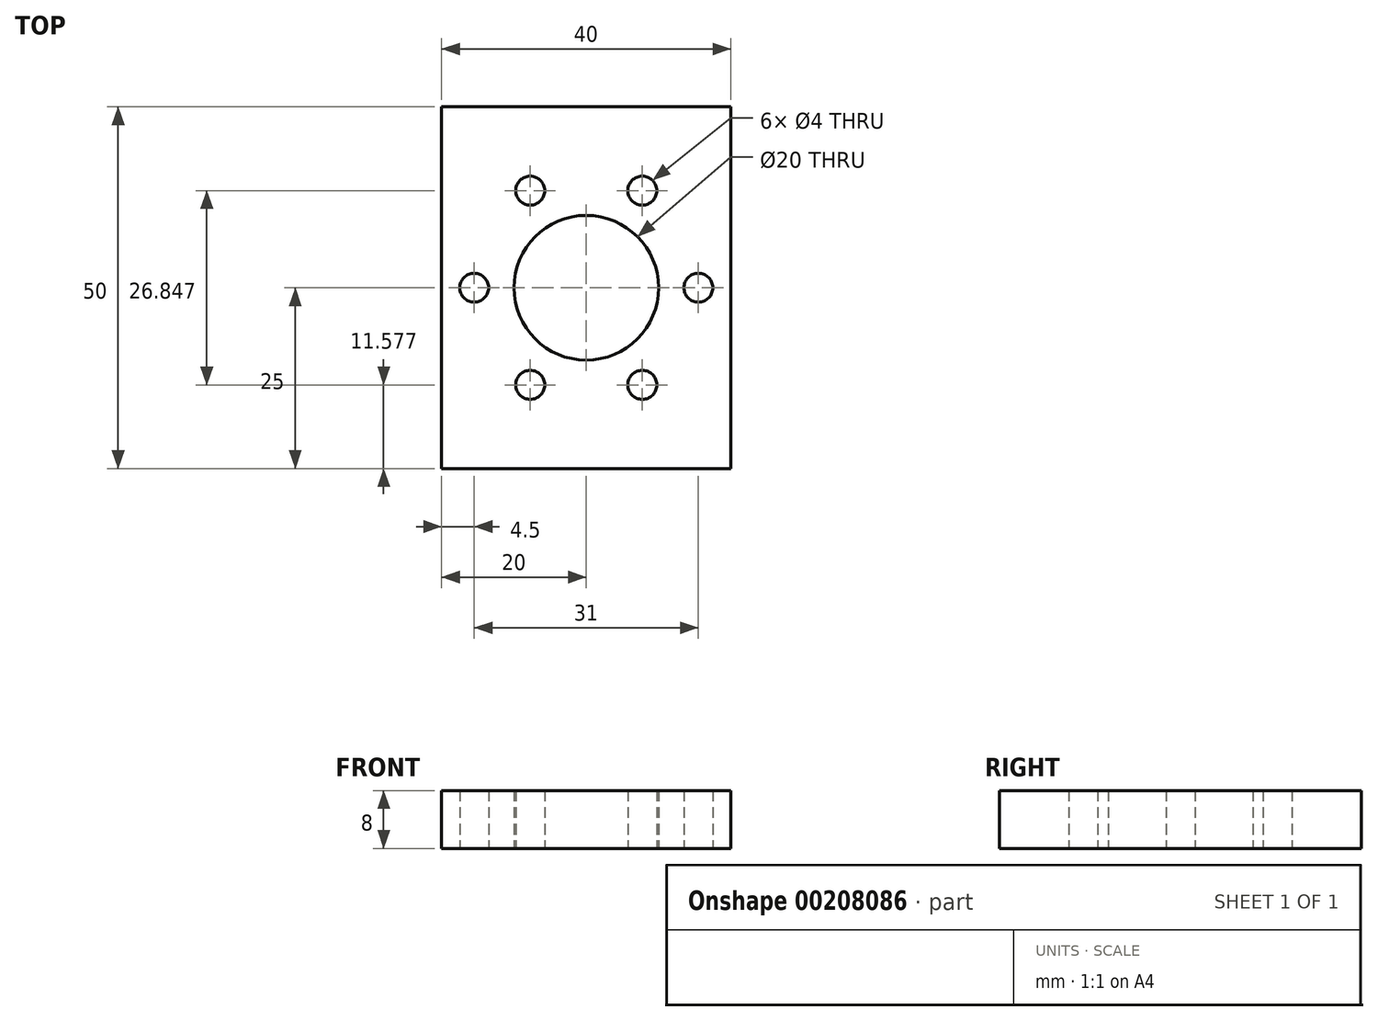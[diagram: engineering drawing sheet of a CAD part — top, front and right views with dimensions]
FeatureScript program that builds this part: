
annotation { "Feature Type Name" : "Feature", "Feature Type Description" : "" }
export const myFeature = defineFeature(function(context is Context, id is Id, definition is map)
    precondition{}
    {
        {
            var Q0;
            Q0=qCreatedBy(makeId("Top.planeOp"),FACE);
            var sketch = newSketch(context, id + "F0", { "sketchPlane" : qUnion([Q0])});
            skLineSegment(sketch, "E0.bottom", {"start": v(21, -21) * mm, "end": v(-21, -21) * mm, "construction": true});
            skLineSegment(sketch, "E0.top", {"start": v(21, 21) * mm, "end": v(-21, 21) * mm, "construction": true});
            skLineSegment(sketch, "E0.left", {"start": v(21, -21) * mm, "end": v(21, 21) * mm, "construction": true});
            skLineSegment(sketch, "E0.right", {"start": v(-21, -21) * mm, "end": v(-21, 21) * mm, "construction": true});
            skPoint(sketch, "E0.middle", {"position": v(0, 0) * mm});
            skLineSegment(sketch, "E1.bottom", {"start": v(15.5, -15.5) * mm, "end": v(-15.5, -15.5) * mm, "construction": true});
            skLineSegment(sketch, "E1.top", {"start": v(15.5, 15.5) * mm, "end": v(-15.5, 15.5) * mm, "construction": true});
            skLineSegment(sketch, "E1.left", {"start": v(15.5, -15.5) * mm, "end": v(15.5, 15.5) * mm, "construction": true});
            skLineSegment(sketch, "E1.right", {"start": v(-15.5, -15.5) * mm, "end": v(-15.5, 15.5) * mm, "construction": true});
            skCircle(sketch, "E2", {"center": v(0, 0) * mm, "radius": 10 * mm});
            skLineSegment(sketch, "E3.bottom", {"start": v(20, -19.5) * mm, "end": v(-20, -19.5) * mm, "construction": true});
            skLineSegment(sketch, "E3.top", {"start": v(20, 19.5) * mm, "end": v(-20, 19.5) * mm, "construction": true});
            skLineSegment(sketch, "E3.left", {"start": v(20, -19.5) * mm, "end": v(20, 19.5) * mm});
            skLineSegment(sketch, "E3.right", {"start": v(-20, -19.5) * mm, "end": v(-20, 19.5) * mm});
            skLineSegment(sketch, "E4", {"start": v(0, 0) * mm, "end": v(-28.5, 0) * mm, "construction": true});
            skLineSegment(sketch, "E5", {"start": v(0, 0) * mm, "end": v(0, 30.15) * mm, "construction": true});
            skPoint(sketch, "E5.endSnap0", {"position": v(0, 19.5) * mm});
            skLineSegment(sketch, "E6", {"start": v(-20, 19.5) * mm, "end": v(-20, 25) * mm});
            skLineSegment(sketch, "E7", {"start": v(-20, 25) * mm, "end": v(20, 25) * mm});
            skLineSegment(sketch, "E8", {"start": v(20, 25) * mm, "end": v(20, 19.5) * mm});
            skLineSegment(sketch, "E9.MirrorCS", {"start": v(-20, -25) * mm, "end": v(20, -25) * mm});
            skLineSegment(sketch, "E10.MirrorCS", {"start": v(-20, -19.5) * mm, "end": v(-20, -25) * mm});
            skLineSegment(sketch, "E11.MirrorCS", {"start": v(20, -25) * mm, "end": v(20, -19.5) * mm});
            skCircle(sketch, "E12", {"center": v(-15.5, 0) * mm, "radius": 2 * mm});
            skCircle(sketch, "E13.1.0", {"center": v(-7.75, -13.42) * mm, "radius": 2 * mm});
            skCircle(sketch, "E13.2.0", {"center": v(7.75, -13.42) * mm, "radius": 2 * mm});
            skCircle(sketch, "E13.3.0", {"center": v(15.5, 0) * mm, "radius": 2 * mm});
            skCircle(sketch, "E13.4.0", {"center": v(7.75, 13.42) * mm, "radius": 2 * mm});
            skCircle(sketch, "E13.5.0", {"center": v(-7.75, 13.42) * mm, "radius": 2 * mm});
            skSolve(sketch);
        }
        {
            var Q0;
            Q0=makeQuery(id+"F0.imprint","IMPRINT",FACE,{"disambiguationData":[TD([[makeQuery(id+"F0.imprint","IMPRINT",EDGE,{"derivedFrom":sQuery(id+"F0.wireOp",EDGE,"E2")}),-1.0]])]});
            extrude(context, id + "F1", {"entities" : qUnion([Q0]), "depth" : 8 * mm, "offsetDistance" : 25 * mm});
        }
    });
